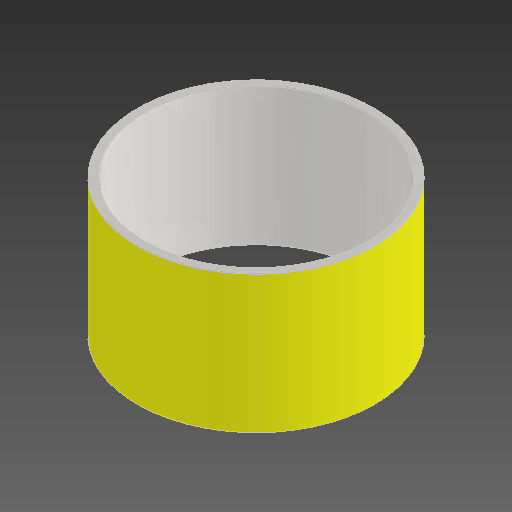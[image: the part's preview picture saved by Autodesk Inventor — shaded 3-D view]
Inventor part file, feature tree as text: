
AUTODESK INVENTOR PART (.ipt)
format: ipt  version: 2020.1 (Build 241239000, 239)  size: 118,784 bytes
history: native  units: mm
features: other x2, extrude x1, chamfer x1, sketch x1
ambient origin geometry x8: Origin, YZ Plane, XZ Plane, XY Plane, X Axis, Y Axis, Z Axis, Center Point
bodies: Solid1 (feature_tree)
feature tree (5):
  other  "Annotations"
  extrude  "Make Metal Ring by Extrusion of Its Profile"  Depth=104.1mm
  chamfer  "Chamfer1"  Distance=104.1mm
  sketch  "Sketch Metal Ring Profile"  dims[d0=179.5mm d1=5.75mm d2=104.1mm d3=0.0mm d4=0.5mm d5=2.0mm d6=45.0deg]
  other  "General Note 1"
